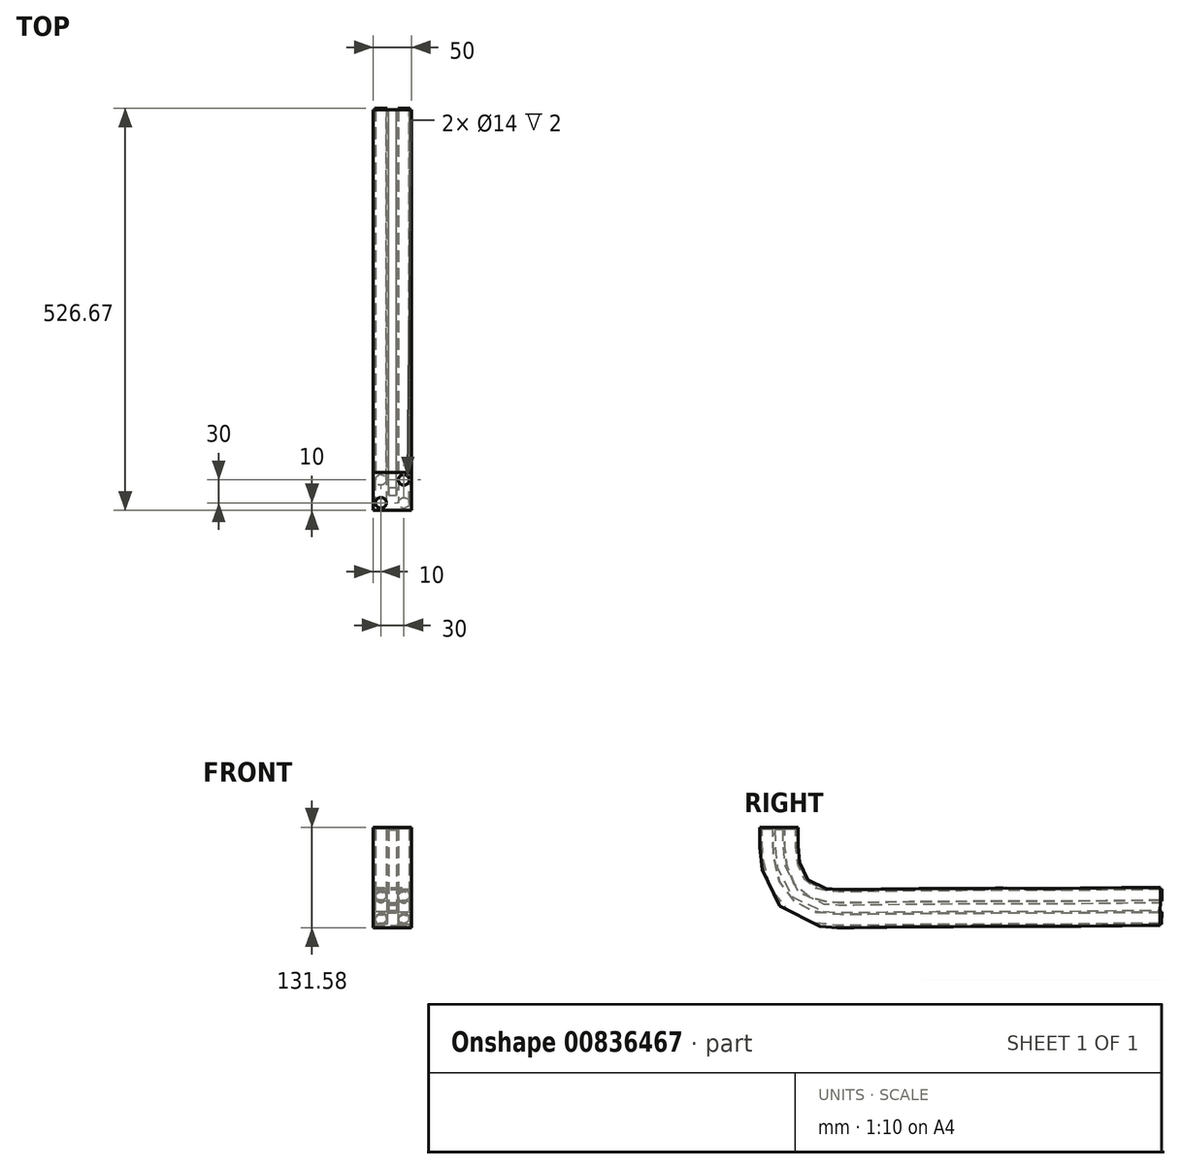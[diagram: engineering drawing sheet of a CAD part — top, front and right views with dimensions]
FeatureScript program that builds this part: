
annotation { "Feature Type Name" : "Feature", "Feature Type Description" : "" }
export const myFeature = defineFeature(function(context is Context, id is Id, definition is map)
    precondition{}
    {
        {
            var Q0;
            Q0=qCreatedBy(makeId("Top.planeOp"),FACE);
            var sketch = newSketch(context, id + "F0", { "sketchPlane" : qUnion([Q0])});
            skLineSegment(sketch, "E0.bottom", {"start": v(-25, 25) * mm, "end": v(25, 25) * mm});
            skLineSegment(sketch, "E0.top", {"start": v(-25, -25) * mm, "end": v(25, -25) * mm});
            skLineSegment(sketch, "E0.left", {"start": v(-25, 25) * mm, "end": v(-25, -25) * mm});
            skLineSegment(sketch, "E0.right", {"start": v(25, 25) * mm, "end": v(25, -25) * mm});
            skPoint(sketch, "E0.middle", {"position": v(0, 0) * mm});
            skLineSegment(sketch, "E1.bottom", {"start": v(-5, 5) * mm, "end": v(5, 5) * mm});
            skLineSegment(sketch, "E1.top", {"start": v(-5, -5) * mm, "end": v(5, -5) * mm});
            skLineSegment(sketch, "E1.left", {"start": v(-5, 5) * mm, "end": v(-5, -5) * mm});
            skLineSegment(sketch, "E1.right", {"start": v(5, 5) * mm, "end": v(5, -5) * mm});
            skCircle(sketch, "E2", {"center": v(-15, 15) * mm, "radius": 7.5 * mm});
            skCircle(sketch, "E3.MirrorC", {"center": v(15, 15) * mm, "radius": 7.5 * mm});
            skCircle(sketch, "E4.MirrorC", {"center": v(-15, -15) * mm, "radius": 7.5 * mm});
            skCircle(sketch, "E5.MirrorC", {"center": v(15, -15) * mm, "radius": 7.5 * mm});
            skCircle(sketch, "E6", {"center": v(-15, 15) * mm, "radius": 7 * mm});
            skCircle(sketch, "E7.MirrorC", {"center": v(15, 15) * mm, "radius": 7 * mm});
            skCircle(sketch, "E8.MirrorC", {"center": v(-15, -15) * mm, "radius": 7 * mm});
            skCircle(sketch, "E9.MirrorC", {"center": v(15, -15) * mm, "radius": 7 * mm});
            skSolve(sketch);
        }
        {
            var Q0;
            Q0=qCreatedBy(makeId("Right.planeOp"),FACE);
            var sketch = newSketch(context, id + "F1", { "sketchPlane" : qUnion([Q0])});
            skFitSpline(sketch, "E10", {"points": [v(49.8, 0) * mm, v(54.95, 50.16) * mm, v(69.9, 56.3) * mm, v(130.07, 56.18) * mm, v(206.61, 55.45) * mm, v(293.74, 54.96) * mm, v(387.97, 54.88) * mm, v(500, 53.86) * mm], "startDerivative": vector(1.87, 524.66) * mm, "endDerivative": vector(549.73, 4.79) * mm});
            skLineSegment(sketch, "E11", {"start": v(0, 0) * mm, "end": v(103.73, 0) * mm});
            skLineSegment(sketch, "E12", {"start": v(103.73, 0) * mm, "end": v(121.19, 0) * mm});
            skFitSpline(sketch, "E13.MirrorCS", {"points": [v(49.8, 0) * mm, v(54.95, -50.16) * mm, v(69.9, -56.3) * mm, v(130.07, -56.18) * mm, v(206.61, -55.45) * mm, v(293.74, -54.96) * mm, v(387.97, -54.88) * mm, v(500, -53.86) * mm], "startDerivative": vector(1.87, -524.66) * mm, "endDerivative": vector(549.73, -4.79) * mm});
            skSolve(sketch);
        }
        {
            var Q0;
            Q0=qCreatedBy(makeId("Top.planeOp"),FACE);
            var sketch = newSketch(context, id + "F2", { "sketchPlane" : qUnion([Q0])});
            skLineSegment(sketch, "E14.bottom", {"start": v(-104.36, -93.42) * mm, "end": v(95.64, -93.42) * mm});
            skLineSegment(sketch, "E14.top", {"start": v(-104.36, 106.58) * mm, "end": v(95.64, 106.58) * mm});
            skLineSegment(sketch, "E14.left", {"start": v(-104.36, -93.42) * mm, "end": v(-104.36, 106.58) * mm});
            skLineSegment(sketch, "E14.right", {"start": v(95.64, -93.42) * mm, "end": v(95.64, 106.58) * mm});
            skSolve(sketch);
        }
        {
            var Q0;
            Q0=makeQuery(id+"F0.imprint","IMPRINT",FACE,{"disambiguationData":[TD([[makeQuery(id+"F0.imprint","IMPRINT",EDGE,{"derivedFrom":sQuery(id+"F0.wireOp",EDGE,"E0.bottom")}),-1.0]])]});
            var Q1;
            Q1=makeQuery(id+"F0.imprint","IMPRINT",FACE,{"disambiguationData":[TD([[makeQuery(id+"F0.imprint","IMPRINT",EDGE,{"derivedFrom":sQuery(id+"F0.wireOp",EDGE,"E8.MirrorC")}),-1.0]])]});
            var Q2;
            Q2=makeQuery(id+"F0.imprint","IMPRINT",FACE,{"disambiguationData":[TD([[makeQuery(id+"F0.imprint","IMPRINT",EDGE,{"derivedFrom":sQuery(id+"F0.wireOp",EDGE,"E6")}),1.0]])]});
            var Q3;
            Q3=makeQuery(id+"F0.imprint","IMPRINT",FACE,{"disambiguationData":[TD([[makeQuery(id+"F0.imprint","IMPRINT",EDGE,{"derivedFrom":sQuery(id+"F0.wireOp",EDGE,"E2")}),1.0]])]});
            var Q4;
            Q4=makeQuery(id+"F0.imprint","IMPRINT",FACE,{"disambiguationData":[TD([[makeQuery(id+"F0.imprint","IMPRINT",EDGE,{"derivedFrom":sQuery(id+"F0.wireOp",EDGE,"E4.MirrorC")}),-1.0]])]});
            var Q5;
            Q5=makeQuery(id+"F0.imprint","IMPRINT",FACE,{"disambiguationData":[TD([[makeQuery(id+"F0.imprint","IMPRINT",EDGE,{"derivedFrom":sQuery(id+"F0.wireOp",EDGE,"E7.MirrorC")}),-1.0]])]});
            var Q6;
            Q6=makeQuery(id+"F0.imprint","IMPRINT",FACE,{"disambiguationData":[TD([[makeQuery(id+"F0.imprint","IMPRINT",EDGE,{"derivedFrom":sQuery(id+"F0.wireOp",EDGE,"E3.MirrorC")}),-1.0]])]});
            var Q7;
            Q7=makeQuery(id+"F0.imprint","IMPRINT",FACE,{"disambiguationData":[TD([[makeQuery(id+"F0.imprint","IMPRINT",EDGE,{"derivedFrom":sQuery(id+"F0.wireOp",EDGE,"E9.MirrorC")}),1.0]])]});
            var Q8;
            Q8=makeQuery(id+"F0.imprint","IMPRINT",FACE,{"disambiguationData":[TD([[makeQuery(id+"F0.imprint","IMPRINT",EDGE,{"derivedFrom":sQuery(id+"F0.wireOp",EDGE,"E5.MirrorC")}),1.0]])]});
            extrude(context, id + "F3", {"entities" : qUnion([Q0, Q1, Q2, Q3, Q4, Q5, Q6, Q7, Q8]), "oppositeDirection" : true, "depth" : 2 * mm, "offsetDistance" : 25 * mm});
        }
        {
            var Q0;
            Q0=makeQuery(id+"F0.imprint","IMPRINT",FACE,{"disambiguationData":[TD([[makeQuery(id+"F0.imprint","IMPRINT",EDGE,{"derivedFrom":sQuery(id+"F0.wireOp",EDGE,"E2")}),1.0]])]});
            var Q1;
            Q1=makeQuery(id+"F0.imprint","IMPRINT",FACE,{"disambiguationData":[TD([[makeQuery(id+"F0.imprint","IMPRINT",EDGE,{"derivedFrom":sQuery(id+"F0.wireOp",EDGE,"E4.MirrorC")}),-1.0]])]});
            var Q2;
            Q2=makeQuery(id+"F0.imprint","IMPRINT",FACE,{"disambiguationData":[TD([[makeQuery(id+"F0.imprint","IMPRINT",EDGE,{"derivedFrom":sQuery(id+"F0.wireOp",EDGE,"E5.MirrorC")}),1.0]])]});
            var Q3;
            Q3=makeQuery(id+"F0.imprint","IMPRINT",FACE,{"disambiguationData":[TD([[makeQuery(id+"F0.imprint","IMPRINT",EDGE,{"derivedFrom":sQuery(id+"F0.wireOp",EDGE,"E3.MirrorC")}),-1.0]])]});
            var Q4;
            Q4=sQuery(id+"F1.wireOp",EDGE,"E13.MirrorCS");
            sweep(context, id + "F4", {"operationType" : NewBodyOperationType.ADD, "profiles" : qUnion([Q0, Q1, Q2, Q3]), "path" : qUnion([Q4])});
        }
        {
            var Q0;
            Q0=makeQuery(id+"F4.opSweep","CAP_FACE",FACE,{"disambiguationData":[OSD([sQuery(id+"F0.wireOp",EDGE,"E4.MirrorC"),sQuery(id+"F0.wireOp",EDGE,"E8.MirrorC"),sQuery(id+"F1.wireOp",VERTEX,"E13.MirrorCS.end")])],"isStart":false});
            var sketch = newSketch(context, id + "F5", { "sketchPlane" : qUnion([Q0])});
            skLineSegment(sketch, "E15.bottom", {"start": v(6.94, -104.63) * mm, "end": v(22.94, -104.63) * mm});
            skLineSegment(sketch, "E15.top", {"start": v(6.94, -120.63) * mm, "end": v(22.94, -120.63) * mm});
            skLineSegment(sketch, "E15.left", {"start": v(6.94, -104.63) * mm, "end": v(6.94, -120.63) * mm});
            skLineSegment(sketch, "E15.right", {"start": v(22.94, -104.63) * mm, "end": v(22.94, -120.63) * mm});
            skLineSegment(sketch, "E16", {"start": v(0, -56.28) * mm, "end": v(0, -160.2) * mm});
            skLineSegment(sketch, "E17.MirrorCS", {"start": v(-6.94, -104.63) * mm, "end": v(-6.94, -120.63) * mm});
            skLineSegment(sketch, "E18.MirrorCS", {"start": v(-6.94, -104.63) * mm, "end": v(-22.94, -104.63) * mm});
            skLineSegment(sketch, "E19.MirrorCS", {"start": v(-6.94, -120.63) * mm, "end": v(-22.94, -120.63) * mm});
            skLineSegment(sketch, "E20.MirrorCS", {"start": v(-22.94, -104.63) * mm, "end": v(-22.94, -120.63) * mm});
            skLineSegment(sketch, "E21", {"start": v(-71.06, -97.58) * mm, "end": v(98.32, -97.58) * mm});
            skLineSegment(sketch, "E22.MirrorCS", {"start": v(-6.94, -90.52) * mm, "end": v(-22.94, -90.52) * mm});
            skLineSegment(sketch, "E23.MirrorCS", {"start": v(-22.94, -90.52) * mm, "end": v(-22.94, -74.52) * mm});
            skLineSegment(sketch, "E24.MirrorCS", {"start": v(-6.94, -74.52) * mm, "end": v(-22.94, -74.52) * mm});
            skLineSegment(sketch, "E25.MirrorCS", {"start": v(-6.94, -90.52) * mm, "end": v(-6.94, -74.52) * mm});
            skLineSegment(sketch, "E26.MirrorCS", {"start": v(6.94, -90.52) * mm, "end": v(22.94, -90.52) * mm});
            skLineSegment(sketch, "E27.MirrorCS", {"start": v(6.94, -90.52) * mm, "end": v(6.94, -74.52) * mm});
            skLineSegment(sketch, "E28.MirrorCS", {"start": v(6.94, -74.52) * mm, "end": v(22.94, -74.52) * mm});
            skLineSegment(sketch, "E29.MirrorCS", {"start": v(22.94, -90.52) * mm, "end": v(22.94, -74.52) * mm});
            skSolve(sketch);
        }
        {
            var Q0;
            Q0=makeQuery(id+"F5.imprint","IMPRINT",FACE,{"disambiguationData":[TD([[makeQuery(id+"F5.imprint","IMPRINT",EDGE,{"derivedFrom":sQuery(id+"F5.wireOp",EDGE,"E26.MirrorCS")}),1.0]])]});
            var Q1;
            Q1=makeQuery(id+"F5.imprint","IMPRINT",FACE,{"disambiguationData":[TD([[makeQuery(id+"F5.imprint","IMPRINT",EDGE,{"derivedFrom":sQuery(id+"F5.wireOp",EDGE,"E22.MirrorCS")}),-1.0]])]});
            var Q2;
            Q2=makeQuery(id+"F5.imprint","IMPRINT",FACE,{"disambiguationData":[TD([[makeQuery(id+"F5.imprint","IMPRINT",EDGE,{"derivedFrom":sQuery(id+"F5.wireOp",EDGE,"E17.MirrorCS")}),-1.0]])]});
            var Q3;
            Q3=makeQuery(id+"F5.imprint","IMPRINT",FACE,{"disambiguationData":[TD([[makeQuery(id+"F5.imprint","IMPRINT",EDGE,{"derivedFrom":sQuery(id+"F5.wireOp",EDGE,"E15.bottom")}),-1.0]])]});
            var Q4;
            Q4=makeQuery(id+"F5.imprint","IMPRINT",FACE,{"disambiguationData":[TD([[makeQuery(id+"F5.imprint","IMPRINT",EDGE,{"derivedFrom":makeQuery(id+"F4.opSweep","CAP_EDGE",EDGE,{"disambiguationData":[OSD([sQuery(id+"F0.wireOp",EDGE,"E8.MirrorC"),sQuery(id+"F1.wireOp",VERTEX,"E13.MirrorCS.end")])],"isStart":false})}),-1.0]])]});
            var Q5;
            {var subQ0=sQuery(id+"F1.wireOp",VERTEX,"E13.MirrorCS.end");Q5=makeQuery(id+"F5.imprint","IMPRINT",FACE,{"disambiguationData":[TD([[makeQuery(id+"F5.imprint","IMPRINT",EDGE,{"derivedFrom":makeQuery(id+"F4.opSweep","CAP_EDGE",EDGE,{"disambiguationData":[OSD([sQuery(id+"F0.wireOp",EDGE,"E4.MirrorC"),subQ0])],"isStart":false})}),1.0]])]});}
            var Q6;
            {var subQ1=sQuery(id+"F5.wireOp",EDGE,"9295ce77-36f8-4b14-b6a5-25fb0c4acafe0.MirrorCS");Q6=makeQuery(id+"F5.imprint","IMPRINT",FACE,{"disambiguationData":[TD([[makeQuery(id+"F5.imprint","IMPRINT",EDGE,{"derivedFrom":subQ1}),-1.0]])]});}
            var Q7;
            Q7=makeQuery(id+"F5.imprint","IMPRINT",FACE,{"disambiguationData":[TD([[makeQuery(id+"F5.imprint","IMPRINT",EDGE,{"derivedFrom":sQuery(id+"F5.wireOp",EDGE,"ur5R90in-naUm-UE7S-Qsad-6jR2aT4kzG23.bottom")}),-1.0]])]});
            extrude(context, id + "F6", {"entities" : qUnion([Q0, Q1, Q2, Q3, Q4, Q5, Q6, Q7]), "operationType" : NewBodyOperationType.ADD, "depth" : 2 * mm, "offsetDistance" : 25 * mm});
        }
        {
            var Q0;
            Q0=makeQuery(id+"F0.imprint","IMPRINT",FACE,{"disambiguationData":[TD([[makeQuery(id+"F0.imprint","IMPRINT",EDGE,{"derivedFrom":sQuery(id+"F0.wireOp",EDGE,"E1.bottom")}),-1.0]])]});
            extrude(context, id + "F7", {"entities" : qUnion([Q0]), "operationType" : NewBodyOperationType.ADD, "oppositeDirection" : true, "depth" : 2 * mm, "offsetDistance" : 25 * mm});
        }
        {
            var Q0;
            Q0=makeQuery(id+"F0.imprint","IMPRINT",FACE,{"disambiguationData":[TD([[makeQuery(id+"F0.imprint","IMPRINT",EDGE,{"derivedFrom":sQuery(id+"F0.wireOp",EDGE,"E1.bottom")}),-1.0]])]});
            extrude(context, id + "F8", {"entities" : qUnion([Q0]), "operationType" : NewBodyOperationType.ADD, "oppositeDirection" : true, "depth" : 3 * mm, "offsetDistance" : 25 * mm});
        }
    });
